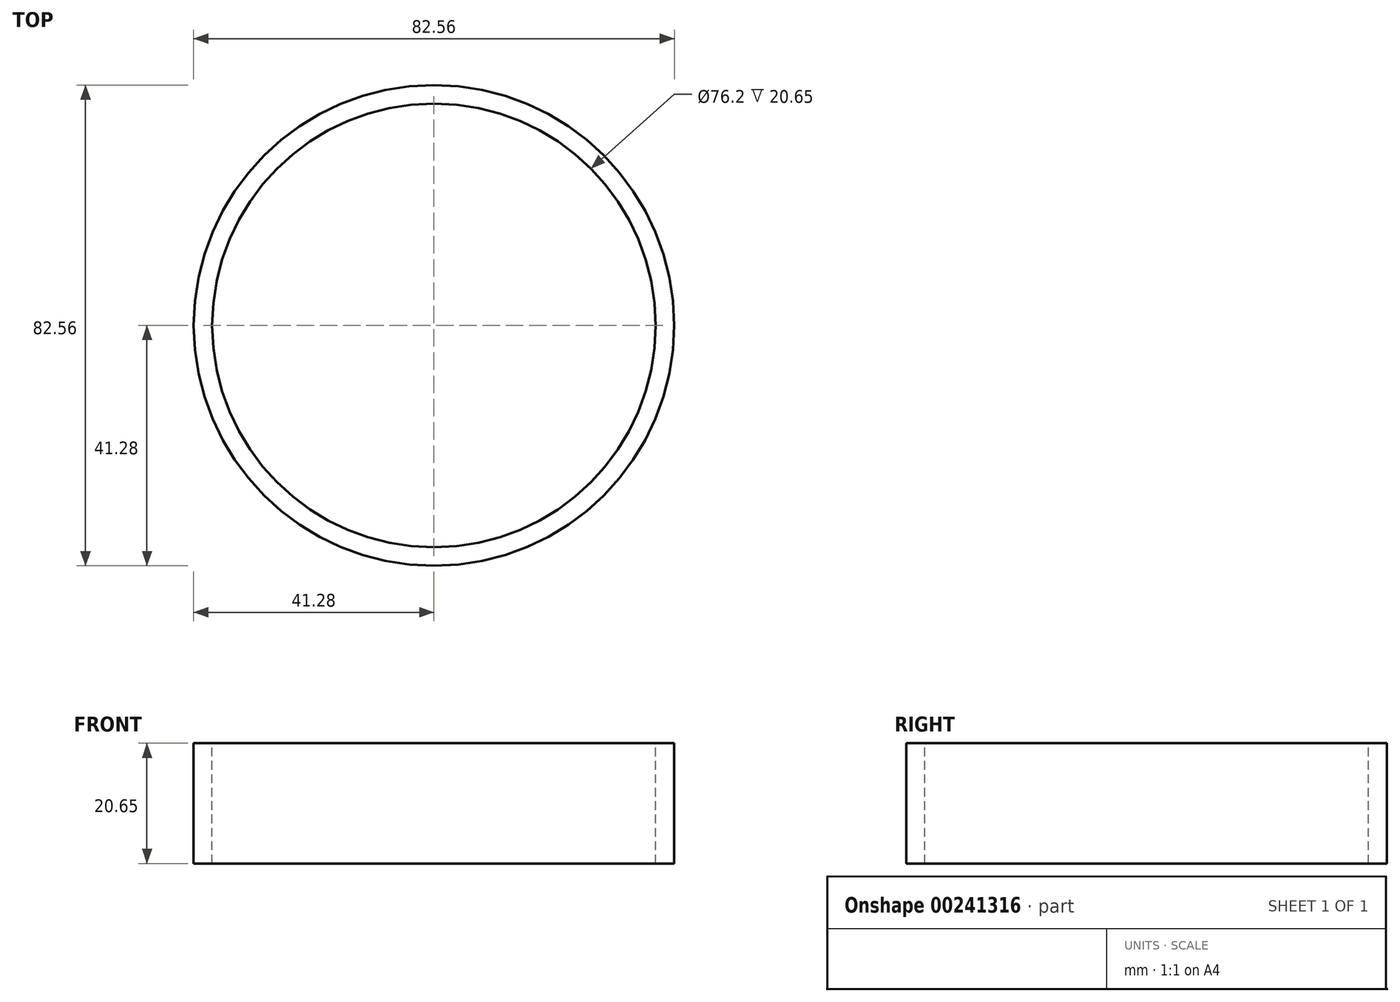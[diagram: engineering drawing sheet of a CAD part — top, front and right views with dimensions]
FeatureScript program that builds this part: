
annotation { "Feature Type Name" : "Feature", "Feature Type Description" : "" }
export const myFeature = defineFeature(function(context is Context, id is Id, definition is map)
    precondition{}
    {
        {
            var Q0;
            Q0=qCreatedBy(makeId("Front.planeOp"),FACE);
            var sketch = newSketch(context, id + "F0", { "sketchPlane" : qUnion([Q0])});
            skLineSegment(sketch, "E0.bottom", {"start": v(0, 0) * mm, "end": v(-3.18, 0) * mm});
            skLineSegment(sketch, "E0.top", {"start": v(0, 20.65) * mm, "end": v(-3.18, 20.65) * mm});
            skLineSegment(sketch, "E0.left", {"start": v(0, 0) * mm, "end": v(0, 20.65) * mm});
            skLineSegment(sketch, "E0.right", {"start": v(-3.18, 0) * mm, "end": v(-3.18, 20.65) * mm});
            skLineSegment(sketch, "E1", {"start": v(38.1, 21.94) * mm, "end": v(38.1, 0) * mm});
            skSolve(sketch);
        }
        {
            var Q0;
            Q0 = qSketchRegion(id + "F0", true);
            var Q1;
            Q1=sQuery(id+"F0.wireOp",EDGE,"E1");
            revolve(context, id + "F1", {"entities" : qUnion([Q0]), "axis" : qUnion([Q1]), "revolveType" : RevolveType.FULL});
        }
    });
